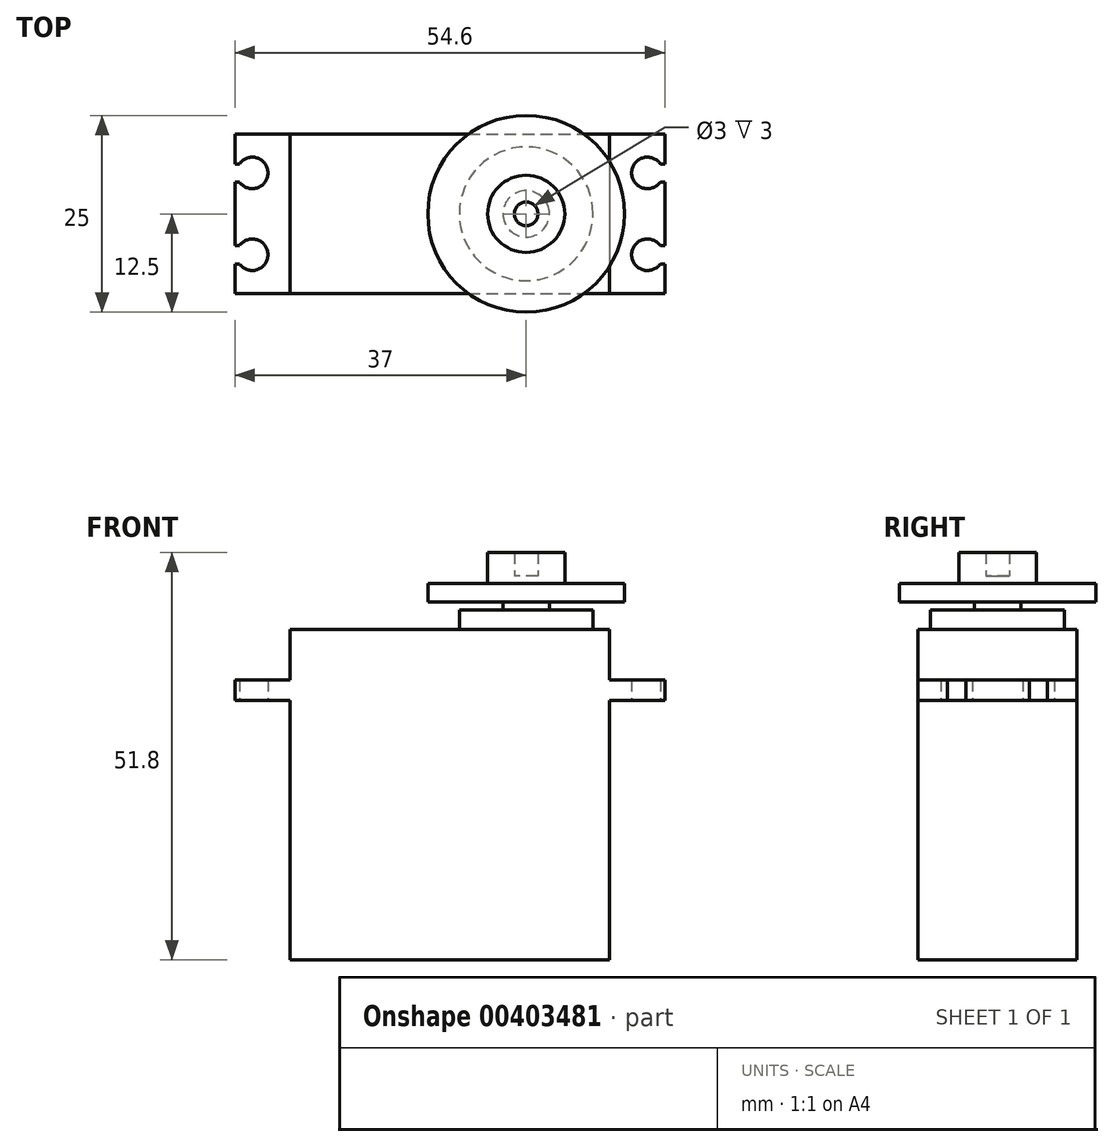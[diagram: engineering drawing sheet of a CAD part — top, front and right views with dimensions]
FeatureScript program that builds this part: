
annotation { "Feature Type Name" : "Feature", "Feature Type Description" : "" }
export const myFeature = defineFeature(function(context is Context, id is Id, definition is map)
    precondition{}
    {
        {
            var Q0;
            Q0=qCreatedBy(makeId("Top.planeOp"),FACE);
            var sketch = newSketch(context, id + "F0", { "sketchPlane" : qUnion([Q0])});
            skLineSegment(sketch, "E0.bottom", {"start": v(-30, 10.1) * mm, "end": v(10.6, 10.1) * mm});
            skLineSegment(sketch, "E0.top", {"start": v(-30, -10.1) * mm, "end": v(10.6, -10.1) * mm});
            skLineSegment(sketch, "E0.left", {"start": v(-30, 10.1) * mm, "end": v(-30, -10.1) * mm});
            skLineSegment(sketch, "E0.right", {"start": v(10.6, 10.1) * mm, "end": v(10.6, -10.1) * mm});
            skCircle(sketch, "E1", {"center": v(0, 0) * mm, "radius": 8.5 * mm});
            skCircle(sketch, "E2", {"center": v(0, 0) * mm, "radius": 2.95 * mm});
            skLineSegment(sketch, "E3.bottom", {"start": v(10.6, 10.1) * mm, "end": v(17.6, 10.1) * mm});
            skLineSegment(sketch, "E3.top", {"start": v(10.6, -10.1) * mm, "end": v(17.6, -10.1) * mm});
            skLineSegment(sketch, "E4.bottom", {"start": v(-30, 10.1) * mm, "end": v(-37, 10.1) * mm});
            skLineSegment(sketch, "E4.top", {"start": v(-30, -10.1) * mm, "end": v(-37, -10.1) * mm});
            skLineSegment(sketch, "E5", {"start": v(-9.7, 11.77) * mm, "end": v(-9.7, -13.9) * mm, "construction": true});
            skPoint(sketch, "E5.startSnap0", {"position": v(-9.7, 10.1) * mm});
            skLineSegment(sketch, "E6", {"start": v(-37, 10.1) * mm, "end": v(-37, 6.35) * mm});
            skArc(sketch, "E7", {"start": v(-36.44, -6.35) * mm, "mid": v(-32.8, -5.2) * mm, "end": v(-36.44, -4.05) * mm});
            skLineSegment(sketch, "E8", {"start": v(-37, -6.35) * mm, "end": v(-36.44, -6.35) * mm});
            skLineSegment(sketch, "E9", {"start": v(-37, -4.05) * mm, "end": v(-36.44, -4.05) * mm});
            skLineSegment(sketch, "E10.MirrorCS", {"start": v(-37, 6.35) * mm, "end": v(-36.44, 6.35) * mm});
            skLineSegment(sketch, "E11.MirrorCS", {"start": v(-37, 4.05) * mm, "end": v(-36.44, 4.05) * mm});
            skArc(sketch, "E12.MirrorC", {"start": v(-36.44, 6.35) * mm, "mid": v(-32.8, 5.2) * mm, "end": v(-36.44, 4.05) * mm});
            skLineSegment(sketch, "E13.MirrorCS", {"start": v(17.6, 4.05) * mm, "end": v(17.04, 4.05) * mm});
            skLineSegment(sketch, "E14.MirrorCS", {"start": v(17.6, 6.35) * mm, "end": v(17.04, 6.35) * mm});
            skLineSegment(sketch, "E15.MirrorCS", {"start": v(17.6, -6.35) * mm, "end": v(17.04, -6.35) * mm});
            skLineSegment(sketch, "E16.MirrorCS", {"start": v(17.6, -4.05) * mm, "end": v(17.04, -4.05) * mm});
            skArc(sketch, "E17.MirrorC", {"start": v(17.04, 6.35) * mm, "mid": v(13.4, 5.2) * mm, "end": v(17.04, 4.05) * mm});
            skArc(sketch, "E18.MirrorC", {"start": v(17.04, -6.35) * mm, "mid": v(13.4, -5.2) * mm, "end": v(17.04, -4.05) * mm});
            skLineSegment(sketch, "E19", {"start": v(17.6, 10.1) * mm, "end": v(17.6, 6.35) * mm});
            skLineSegment(sketch, "E20.trimOffspring", {"start": v(-37, -6.35) * mm, "end": v(-37, -10.1) * mm});
            skLineSegment(sketch, "E21.trimOffspring", {"start": v(-37, 4.05) * mm, "end": v(-37, -4.05) * mm});
            skLineSegment(sketch, "E22.trimOffspring", {"start": v(17.6, 4.05) * mm, "end": v(17.6, -4.05) * mm});
            skLineSegment(sketch, "E23.trimOffspring", {"start": v(17.6, -6.35) * mm, "end": v(17.6, -10.1) * mm});
            skSolve(sketch);
        }
        {
            var Q0;
            {var subQ0=sQuery(id+"F0.wireOp",EDGE,"E0.left");Q0=makeQuery(id+"F0.imprint","IMPRINT",FACE,{"disambiguationData":[TD([[makeQuery(id+"F0.imprint","IMPRINT",EDGE,{"derivedFrom":subQ0}),1.0]])]});}
            var Q1;
            Q1=makeQuery(id+"F0.imprint","IMPRINT",FACE,{"disambiguationData":[TD([[makeQuery(id+"F0.imprint","IMPRINT",EDGE,{"derivedFrom":sQuery(id+"F0.wireOp",EDGE,"E2")}),-1.0]])]});
            var Q2;
            Q2=makeQuery(id+"F0.imprint","IMPRINT",FACE,{"disambiguationData":[TD([[makeQuery(id+"F0.imprint","IMPRINT",EDGE,{"derivedFrom":sQuery(id+"F0.wireOp",EDGE,"E2")}),1.0]])]});
            var Q3;
            {var subQ1=sQuery(id+"F0.wireOp",EDGE,"E0.bottom");var subQ3=sQuery(id+"F0.wireOp",EDGE,"E1");var subQ4=makeQuery(id+"F0.imprint","INTERSECT",VERTEX,{"derivedFrom":[subQ1,subQ3]});Q3=makeQuery(id+"F0.imprint","IMPRINT",FACE,{"disambiguationData":[TD([[makeQuery(id+"F0.imprint","IMPRINT",EDGE,{"disambiguationData":[TD([[subQ4,1.0]])],"derivedFrom":subQ3}),-1.0]])]});}
            var Q4;
            {var subQ1=sQuery(id+"F0.wireOp",EDGE,"E0.top");var subQ3=sQuery(id+"F0.wireOp",EDGE,"E1");var subQ4=makeQuery(id+"F0.imprint","INTERSECT",VERTEX,{"derivedFrom":[subQ1,subQ3]});Q4=makeQuery(id+"F0.imprint","IMPRINT",FACE,{"disambiguationData":[TD([[makeQuery(id+"F0.imprint","IMPRINT",EDGE,{"disambiguationData":[TD([[subQ4,-1.0]])],"derivedFrom":subQ3}),-1.0]])]});}
            extrude(context, id + "F1", {"entities" : qUnion([Q0, Q1, Q2, Q3, Q4]), "oppositeDirection" : true, "depth" : (42 - 9) * mm, "hasSecondDirection" : true, "secondDirectionOppositeDirection" : false, "secondDirectionDepth" : 9 * mm});
        }
        {
            var Q0;
            Q0=makeQuery(id+"F0.imprint","IMPRINT",FACE,{"disambiguationData":[TD([[makeQuery(id+"F0.imprint","IMPRINT",EDGE,{"derivedFrom":sQuery(id+"F0.wireOp",EDGE,"E4.bottom")}),1.0]])]});
            var Q1;
            {var subQ3=sQuery(id+"F0.wireOp",EDGE,"E3.bottom");Q1=makeQuery(id+"F0.imprint","IMPRINT",FACE,{"disambiguationData":[TD([[makeQuery(id+"F0.imprint","IMPRINT",EDGE,{"derivedFrom":subQ3}),-1.0]])]});}
            extrude(context, id + "F2", {"entities" : qUnion([Q0, Q1]), "operationType" : NewBodyOperationType.ADD, "depth" : 2.6 * mm});
        }
        {
            var Q0;
            Q0=makeQuery(id+"F0.imprint","IMPRINT",FACE,{"disambiguationData":[TD([[makeQuery(id+"F0.imprint","IMPRINT",EDGE,{"derivedFrom":sQuery(id+"F0.wireOp",EDGE,"E2")}),-1.0]])]});
            var Q1;
            Q1=makeQuery(id+"F0.imprint","IMPRINT",FACE,{"disambiguationData":[TD([[makeQuery(id+"F0.imprint","IMPRINT",EDGE,{"derivedFrom":sQuery(id+"F0.wireOp",EDGE,"E2")}),1.0]])]});
            extrude(context, id + "F3", {"entities" : qUnion([Q0, Q1]), "operationType" : NewBodyOperationType.ADD, "depth" : (9 + 2.5) * mm});
        }
        {
            var Q0;
            Q0=makeQuery(id+"F0.imprint","IMPRINT",FACE,{"disambiguationData":[TD([[makeQuery(id+"F0.imprint","IMPRINT",EDGE,{"derivedFrom":sQuery(id+"F0.wireOp",EDGE,"E2")}),1.0]])]});
            extrude(context, id + "F4", {"entities" : qUnion([Q0]), "operationType" : NewBodyOperationType.ADD, "depth" : (9 + 2.5 + 4.3) * mm});
        }
        {
            var Q0;
            Q0=makeQuery(id+"F4.opExtrude","CAP_FACE",FACE,{"disambiguationData":[OSD([sQuery(id+"F0.wireOp",EDGE,"E2")])],"isStart":false});
            var sketch = newSketch(context, id + "F5", { "sketchPlane" : qUnion([Q0])});
            skCircle(sketch, "E24.0", {"center": v(0, 0) * mm, "radius": 2.95 * mm});
            skCircle(sketch, "E25", {"center": v(0, 0) * mm, "radius": 4.9 * mm});
            skCircle(sketch, "E26", {"center": v(0, 0) * mm, "radius": 12.5 * mm});
            skCircle(sketch, "E27", {"center": v(0, 0) * mm, "radius": 1.5 * mm});
            skSolve(sketch);
        }
        {
            var Q0;
            Q0=makeQuery(id+"F5.imprint","IMPRINT",FACE,{"disambiguationData":[TD([[makeQuery(id+"F5.imprint","IMPRINT",EDGE,{"derivedFrom":sQuery(id+"F5.wireOp",EDGE,"E24.0")}),-1.0]])]});
            extrude(context, id + "F6", {"entities" : qUnion([Q0]), "oppositeDirection" : true, "depth" : 3.3 * mm, "hasSecondDirection" : true, "secondDirectionOppositeDirection" : false, "secondDirectionDepth" : 3 * mm, "offsetDistance" : 25 * mm});
        }
        {
            var Q0;
            Q0=makeQuery(id+"F5.imprint","IMPRINT",FACE,{"disambiguationData":[TD([[makeQuery(id+"F5.imprint","IMPRINT",EDGE,{"derivedFrom":sQuery(id+"F5.wireOp",EDGE,"E25")}),-1.0]])]});
            var Q1;
            Q1=makeQuery(id+"F5.imprint","IMPRINT",FACE,{"disambiguationData":[TD([[makeQuery(id+"F5.imprint","IMPRINT",EDGE,{"derivedFrom":sQuery(id+"F5.wireOp",EDGE,"E24.0")}),-1.0]])]});
            extrude(context, id + "F7", {"entities" : qUnion([Q0, Q1]), "operationType" : NewBodyOperationType.ADD, "oppositeDirection" : true, "depth" : 3.3 * mm, "hasSecondDirection" : true, "secondDirectionOppositeDirection" : true, "secondDirectionDepth" : (3.3 - 2.35) * mm, "offsetDistance" : 25 * mm});
        }
        {
            var Q0;
            Q0=makeQuery(id+"F5.imprint","IMPRINT",FACE,{"disambiguationData":[TD([[makeQuery(id+"F5.imprint","IMPRINT",EDGE,{"derivedFrom":sQuery(id+"F5.wireOp",EDGE,"E24.0")}),1.0]])]});
            extrude(context, id + "F8", {"entities" : qUnion([Q0]), "operationType" : NewBodyOperationType.ADD, "depth" : 3 * mm, "offsetDistance" : 25 * mm});
        }
    });
